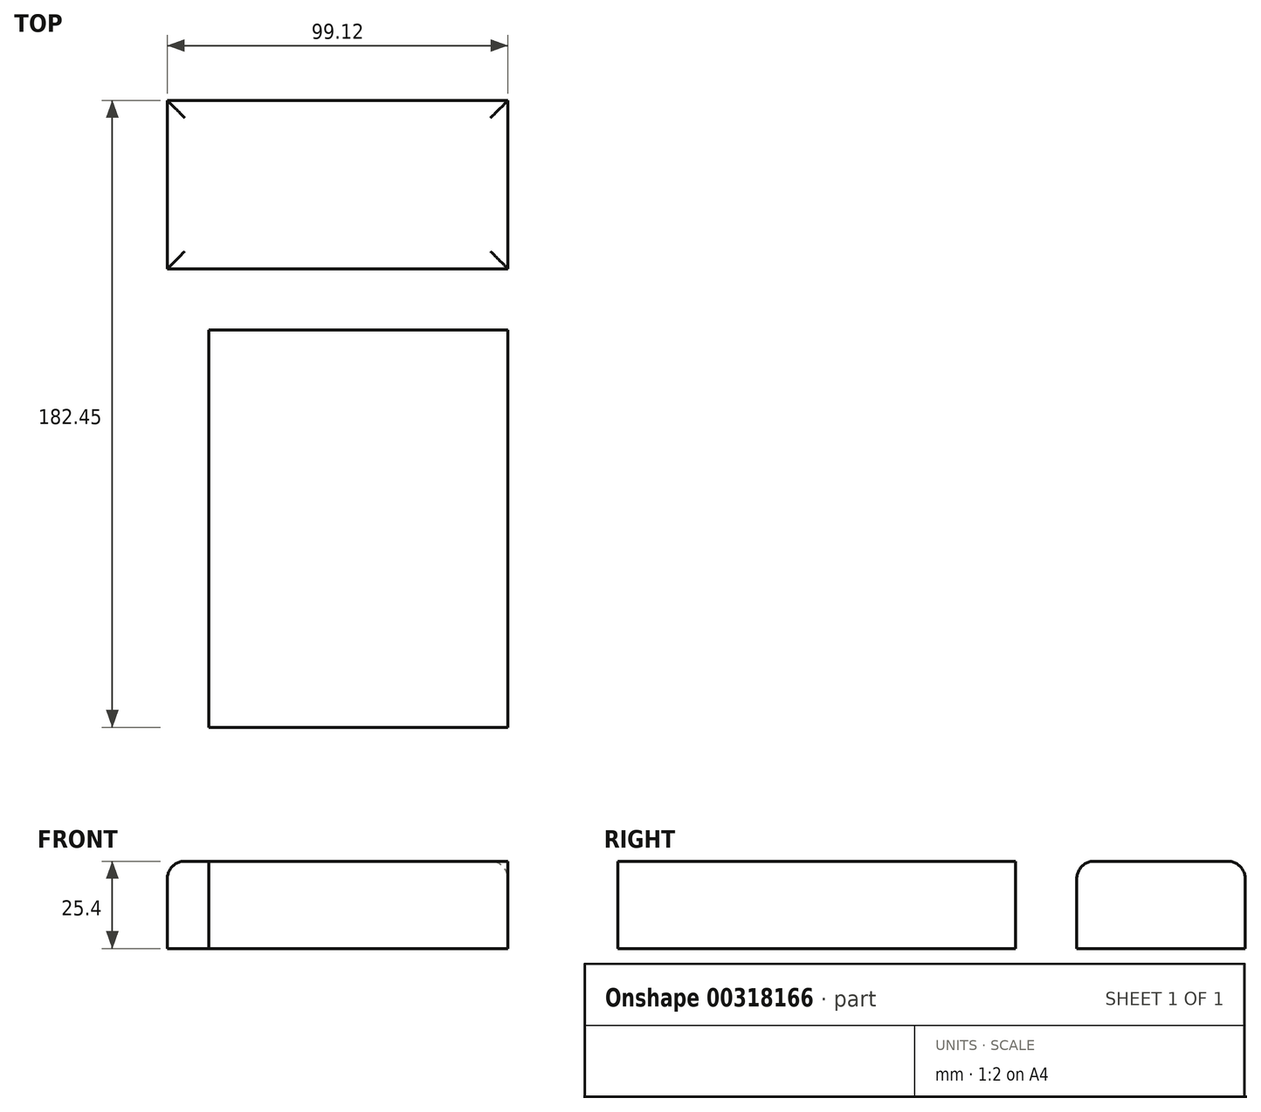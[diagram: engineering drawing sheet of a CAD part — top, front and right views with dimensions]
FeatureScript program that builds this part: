
annotation { "Feature Type Name" : "Feature", "Feature Type Description" : "" }
export const myFeature = defineFeature(function(context is Context, id is Id, definition is map)
    precondition{}
    {
        {
            var Q0;
            Q0=qCreatedBy(makeId("Top.planeOp"),FACE);
            var sketch = newSketch(context, id + "F0", { "sketchPlane" : qUnion([Q0])});
            skLineSegment(sketch, "E0.bottom", {"start": v(0, 0) * mm, "end": v(87.02, 0) * mm});
            skLineSegment(sketch, "E0.top", {"start": v(0, 115.64) * mm, "end": v(87.02, 115.64) * mm});
            skLineSegment(sketch, "E0.left", {"start": v(0, 0) * mm, "end": v(0, 115.64) * mm});
            skLineSegment(sketch, "E0.right", {"start": v(87.02, 0) * mm, "end": v(87.02, 115.64) * mm});
            skLineSegment(sketch, "E1.bottom", {"start": v(-12.1, 182.45) * mm, "end": v(87.02, 182.45) * mm});
            skLineSegment(sketch, "E1.top", {"start": v(-12.1, 133.45) * mm, "end": v(87.02, 133.45) * mm});
            skLineSegment(sketch, "E1.left", {"start": v(-12.1, 182.45) * mm, "end": v(-12.1, 133.45) * mm});
            skLineSegment(sketch, "E1.right", {"start": v(87.02, 182.45) * mm, "end": v(87.02, 133.45) * mm});
            skSolve(sketch);
        }
        {
            var Q0;
            Q0=makeQuery(id+"F0.imprint","IMPRINT",FACE,{"disambiguationData":[TD([[makeQuery(id+"F0.imprint","IMPRINT",EDGE,{"derivedFrom":sQuery(id+"F0.wireOp",EDGE,"E0.bottom")}),1.0]])]});
            var Q1;
            Q1=makeQuery(id+"F0.imprint","IMPRINT",FACE,{"disambiguationData":[TD([[makeQuery(id+"F0.imprint","IMPRINT",EDGE,{"derivedFrom":sQuery(id+"F0.wireOp",EDGE,"E1.bottom")}),-1.0]])]});
            extrude(context, id + "F1", {"entities" : qUnion([Q0, Q1]), "depth" : 25.4 * mm});
        }
        {
            var Q0;
            Q0=makeQuery(id+"F1.opExtrude","CAP_FACE",FACE,{"disambiguationData":[OSD([sQuery(id+"F0.wireOp",EDGE,"E1.bottom"),sQuery(id+"F0.wireOp",EDGE,"E1.top"),sQuery(id+"F0.wireOp",EDGE,"E1.left"),sQuery(id+"F0.wireOp",EDGE,"E1.right")])],"isStart":false});
            fillet(context, id + "F2", {"entities" : qUnion([Q0]), "radius" : 5.08 * mm, "tangentPropagation" : true, "allowEdgeOverflow" : false});
        }
    });
